# Revit family: Air-Curtain_Specialty_PoweredAire_HDX-Hazardous
name_source: partatom
category: Mechanical Equipment
units: mm (PartAtom-declared; Revit-internal decimal feet)

## family parameters
Cut with Voids When Loaded = No
Host = Face
Maintain Annotation Orientation = No
OmniClass Number = 23.75.35.17.21
OmniClass Title = Air Curtains
Part Type = Normal
Room Calculation Point = No
Round Connector Dimension = Use Diameter
Shared = No

## types (7) — shared parameters
Assembly Code = D3090400
Construction Details = http://www.arcat.com
Default Elevation = 0' - 0"
Green Building-LEED = http://www.arcat.com
HVAC_Temperature Rise = 0 °F
Heating Element Load = 0 W
Keynote = 23 34 33
Manufacturer = Powered Aire, Inc
Manufacturer Fax = 724-588-3371
Manufacturer Website = http://www.poweredaire.com
Max Height = 17' - 0"
Motor HP = 3
Motor RPM = 1160
Power Rating = 0 W
Product Data = http://www.arcat.com
Revision = R1_2016-08
Sales Information = http://www.poweredaire.com
Specification = http://www.arcat.com
Standards Conformance = Class I C and D  ;  Class II F and G  ;  Made in USA
URL = http://www.poweredaire.com
Unit Depth = 2' - 3 1/4"
Unit Height = 1' - 9"
Unit Width Notes = Other Widths available.
zero-valued in all types: Expected Lifespan (Years), Maintenance Schedule (Months), Warranty Duration (Years)

## per-type parameters (varying)
| type | Description | HVAC_Outlet Velocity | HVAC_Outlet Velocity Uniformity | HVAC_Outlet Volume | Model | Motor Count | Mounting Width | Nozzle Width | Sound Pressure | Unit Weight | Unit Width |
| 192'' Nozzle | Powered Aire Unheated Hazardous Area Air Curtain - HDX-3-192 as Specified | 6200 FPM | 0.863 | 15700 CFM | HDX-3-192 | 3 | 16' - 1 3/4" | 16' - 0 1/4" | >69 dBA | 1170 | 16' - 3 1/4" |
| 180'' Nozzle | Powered Aire Unheated Hazardous Area Air Curtain - HDX-3-180 as Specified | 6200 FPM | 0.863 | 15000 CFM | HDX-3-180 | 3 | 15' - 1 3/4" | 15' - 0 1/4" | >69 dBA | 1150 | 15' - 3 1/4" |
| 144'' Nozzle | Powered Aire Unheated Hazardous Area Air Curtain - HDX-2-144 as Specified | 5900 FPM | 0.863 | 11200 CFM | HDX-2-144 | 2 | 12' - 1 5/8" | 12' - 0 1/8" | >69 dBA | 830 | 12' - 3 1/8" |
| 132'' Nozzle | Powered Aire Unheated Hazardous Area Air Curtain - HDX-2-132 as Specified | 5900 FPM | 0.863 | 10400 CFM | HDX-2-132 | 2 | 11' - 1 5/8" | 11' - 0 1/8" | >69 dBA | 805 | 11' - 3 1/8" |
| 120'' Nozzle | Powered Aire Unheated Hazardous Area Air Curtain - HDX-2-120 as Specified | 5800 FPM | 0.92 | 9700 CFM | HDX-2-120 | 2 | 10' - 1 5/8" | 10' - 0 1/8" | >69 dBA | 785 | 10' - 3 1/8" |
| 72'' Nozzle | Powered Aire Unheated Hazardous Area Air Curtain - HDX-1-72 as Specified | 5900 FPM | 0.863 | 5600 CFM | HDX-1-72 | 1 | 6' - 1 1/2" | 6' - 0" | 69 dBA | 420 | 6' - 3" |
| 60'' Nozzle | Powered Aire Unheated Hazardous Area Air Curtain - HDX-1-60 as Specified | 5800 FPM | 0.92 | 4900 CFM | HDX-1-60 | 1 | 5' - 1 1/2" | 5' - 0" | 69 dBA | 400 | 5' - 3" |

## geometry (parser evidence)
native form markers: Sweep x3
no freeform markers — native parametric forms only
